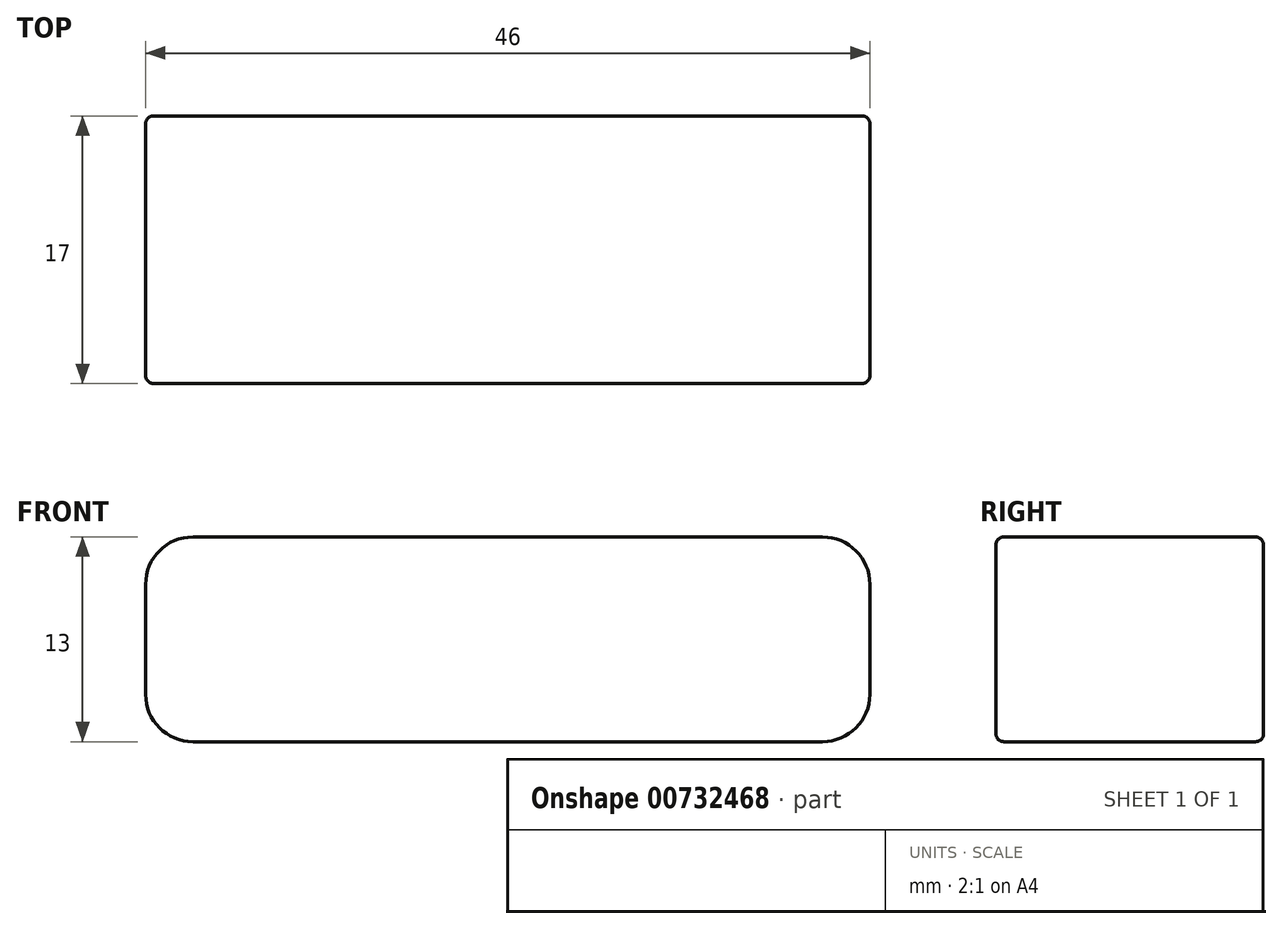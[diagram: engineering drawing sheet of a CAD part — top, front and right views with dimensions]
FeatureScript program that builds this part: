
annotation { "Feature Type Name" : "Feature", "Feature Type Description" : "" }
export const myFeature = defineFeature(function(context is Context, id is Id, definition is map)
    precondition{}
    {
        {
            var Q0;
            Q0=qCreatedBy(makeId("Right.planeOp"),FACE);
            var sketch = newSketch(context, id + "F0", { "sketchPlane" : qUnion([Q0])});
            skLineSegment(sketch, "E0.bottom", {"start": v(0, 0) * mm, "end": v(17, 0) * mm});
            skLineSegment(sketch, "E0.top", {"start": v(0, -13) * mm, "end": v(17, -13) * mm});
            skLineSegment(sketch, "E0.left", {"start": v(0, 0) * mm, "end": v(0, -13) * mm});
            skLineSegment(sketch, "E0.right", {"start": v(17, 0) * mm, "end": v(17, -13) * mm});
            skSolve(sketch);
        }
        {
            var Q0;
            Q0=makeQuery(id+"F0.imprint","IMPRINT",FACE,{"disambiguationData":[TD([[makeQuery(id+"F0.imprint","IMPRINT",EDGE,{"derivedFrom":sQuery(id+"F0.wireOp",EDGE,"E0.bottom")}),-1.0]])]});
            extrude(context, id + "F1", {"entities" : qUnion([Q0]), "depth" : 46 * mm, "offsetDistance" : 25 * mm});
        }
        {
            var Q0;
            Q0=makeQuery(id+"F1.opExtrude","CAP_EDGE",EDGE,{"disambiguationData":[OSD([sQuery(id+"F0.wireOp",EDGE,"E0.bottom")])],"isStart":false});
            var Q1;
            Q1=makeQuery(id+"F1.opExtrude","CAP_EDGE",EDGE,{"disambiguationData":[OSD([sQuery(id+"F0.wireOp",EDGE,"E0.top")])],"isStart":false});
            var Q2;
            Q2=makeQuery(id+"F1.opExtrude","CAP_EDGE",EDGE,{"disambiguationData":[OSD([sQuery(id+"F0.wireOp",EDGE,"E0.bottom")])],"isStart":true});
            var Q3;
            Q3=makeQuery(id+"F1.opExtrude","CAP_EDGE",EDGE,{"disambiguationData":[OSD([sQuery(id+"F0.wireOp",EDGE,"E0.top")])],"isStart":true});
            fillet(context, id + "F2", {"entities" : qUnion([Q0, Q1, Q2, Q3]), "radius" : 3 * mm, "tangentPropagation" : true, "allowEdgeOverflow" : false});
        }
        {
            var Q0;
            Q0=makeQuery(id+"F1.opExtrude","SWEPT_EDGE",EDGE,{"disambiguationData":[OSD([sQuery(id+"F0.wireOp",EDGE,"E0.bottom"),sQuery(id+"F0.wireOp",EDGE,"E0.left")])]});
            var Q1;
            Q1=makeQuery(id+"F1.opExtrude","SWEPT_EDGE",EDGE,{"disambiguationData":[OSD([sQuery(id+"F0.wireOp",EDGE,"E0.bottom"),sQuery(id+"F0.wireOp",EDGE,"E0.right")])]});
            fillet(context, id + "F3", {"entities" : qUnion([Q0, Q1]), "radius" : 0.5 * mm, "tangentPropagation" : true, "allowEdgeOverflow" : false});
        }
    });
